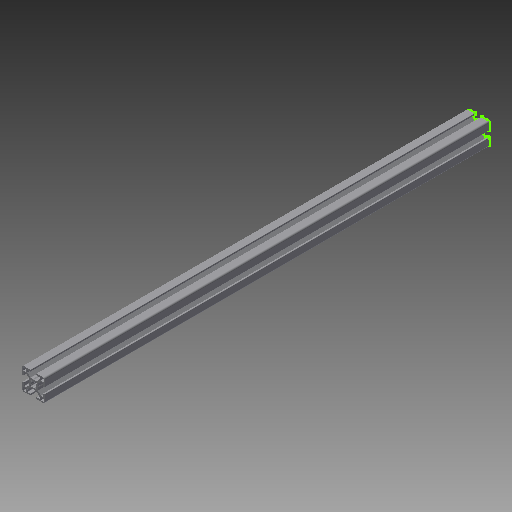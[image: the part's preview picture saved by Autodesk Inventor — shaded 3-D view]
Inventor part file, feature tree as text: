
AUTODESK INVENTOR PART (.ipt)
format: ipt  version: 2018 (Build 220112000, 112)  size: 351,744 bytes
history: native  units: mm
features: sketch x2, extrude x1, plane x1
ambient origin geometry x8: Origin, YZ Plane, XZ Plane, XY Plane, X Axis, Y Axis, Z Axis, Center Point
bodies: Solid1 (feature_tree)
feature tree (4):
  sketch  "Sketch1"  dims[d0=600.0mm d1=0.0mm]
  extrude  "Extrusion1"  [1 undecoded]
  plane  "Work Plane1"
  sketch  "Sketch3"
note: 1 required parameter value undecoded (feature->parameter linkage not recoverable at this tier; creation-order binding heuristic only, values carry confidence <= 0.55)
